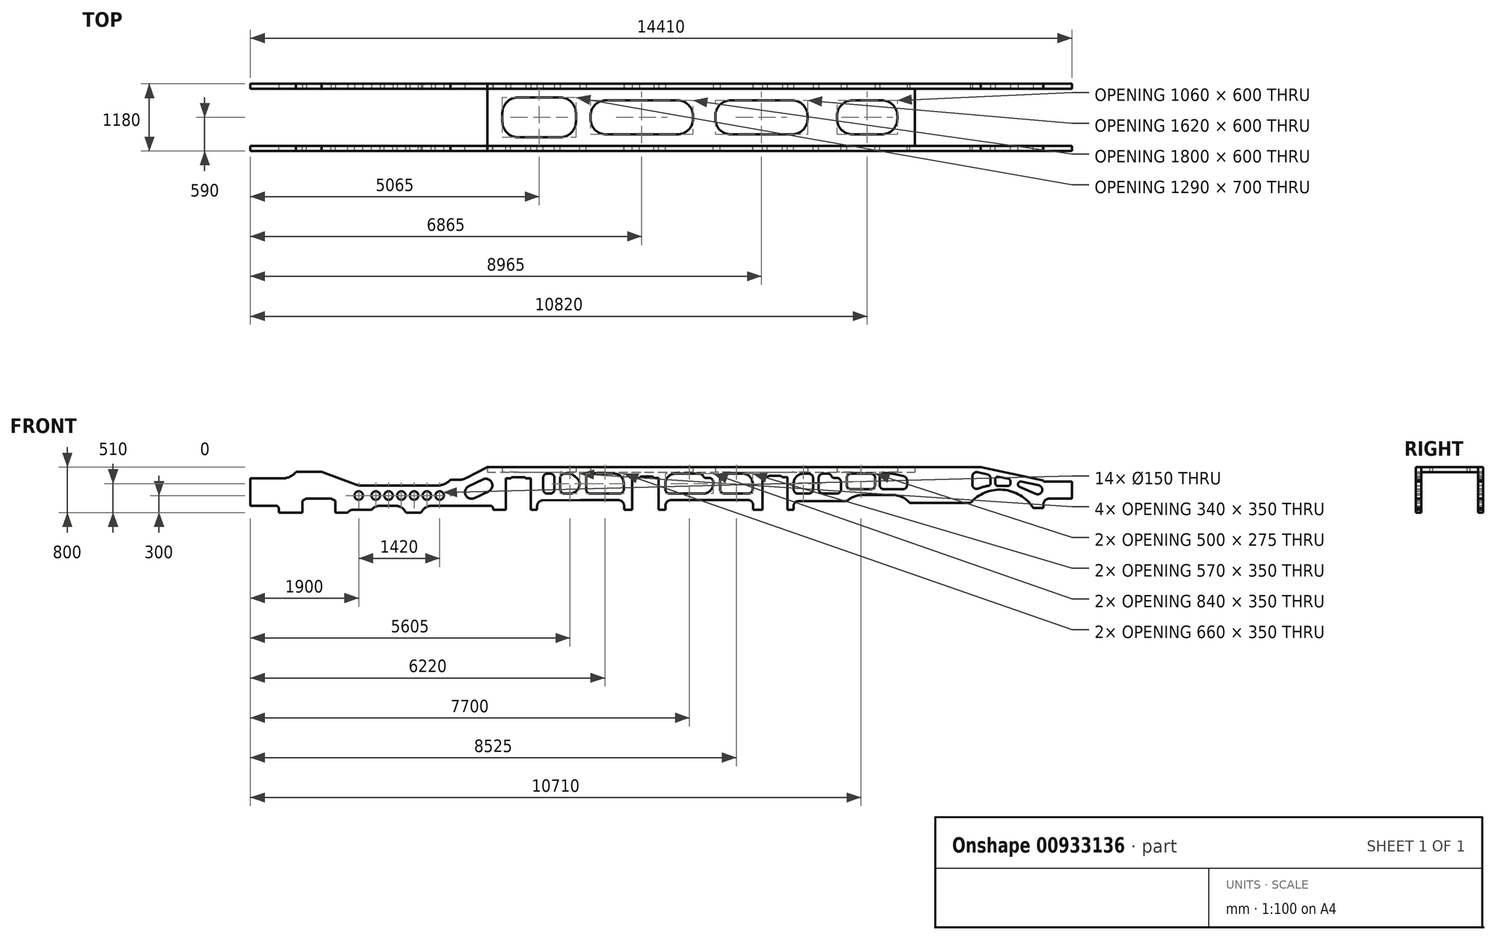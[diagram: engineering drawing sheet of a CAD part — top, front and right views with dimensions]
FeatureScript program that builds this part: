
annotation { "Feature Type Name" : "Feature", "Feature Type Description" : "" }
export const myFeature = defineFeature(function(context is Context, id is Id, definition is map)
    precondition{}
    {
        {
            var Q0;
            Q0=qCreatedBy(makeId("Front.planeOp"),FACE);
            var sketch = newSketch(context, id + "F0", { "sketchPlane" : qUnion([Q0])});
            skLineSegment(sketch, "E0", {"start": v(0, 0) * mm, "end": v(1200, 0) * mm, "construction": true});
            skLineSegment(sketch, "E1", {"start": v(1200, 0) * mm, "end": v(1200, 1949.78) * mm, "construction": true});
            skCircle(sketch, "E2", {"center": v(1200, 625) * mm, "radius": 625 * mm, "construction": true});
            skLineSegment(sketch, "E3", {"start": v(1200, 0) * mm, "end": v(4700, 0) * mm, "construction": true});
            skSolve(sketch);
        }
        {
            var Q0;
            Q0=qCreatedBy(makeId("Front.planeOp"),FACE);
            var sketch = newSketch(context, id + "F1", { "sketchPlane" : qUnion([Q0])});
            skLineSegment(sketch, "E4", {"start": v(800, 1370) * mm, "end": v(1250, 1370) * mm});
            skLineSegment(sketch, "E5", {"start": v(0, 770) * mm, "end": v(450, 770) * mm});
            skLineSegment(sketch, "E6", {"start": v(0, 770) * mm, "end": v(0, 1250) * mm});
            skLineSegment(sketch, "E7", {"start": v(500, 720) * mm, "end": v(500, 650) * mm});
            skLineSegment(sketch, "E8", {"start": v(500, 650) * mm, "end": v(912.5, 650) * mm});
            skLineSegment(sketch, "E9", {"start": v(912.5, 650) * mm, "end": v(912.5, 858.14) * mm});
            skLineSegment(sketch, "E10", {"start": v(912.5, 858.14) * mm, "end": v(985, 900) * mm});
            skLineSegment(sketch, "E11", {"start": v(985, 900) * mm, "end": v(1415, 900) * mm});
            skLineSegment(sketch, "E12", {"start": v(1415, 900) * mm, "end": v(1487.5, 858.14) * mm});
            skLineSegment(sketch, "E13", {"start": v(1487.5, 858.14) * mm, "end": v(1487.5, 650) * mm});
            skLineSegment(sketch, "E14", {"start": v(1487.5, 650) * mm, "end": v(1708.4, 650) * mm});
            skLineSegment(sketch, "E15", {"start": v(1795, 700) * mm, "end": v(2123.01, 700) * mm});
            skLineSegment(sketch, "E16", {"start": v(1200, 0) * mm, "end": v(1200, 1370) * mm, "construction": true});
            skLineSegment(sketch, "E17", {"start": v(2728.3, 650) * mm, "end": v(2996.7, 650) * mm});
            skLineSegment(sketch, "E18", {"start": v(2275, 770) * mm, "end": v(2545, 770) * mm});
            skPoint(sketch, "E19.visualSharp", {"position": v(500, 770) * mm});
            skArc(sketch, "E19.filletArc", {"start": v(500, 720) * mm, "mid": v(485.36, 755.36) * mm, "end": v(450, 770) * mm});
            skArc(sketch, "E20", {"start": v(1708.4, 650) * mm, "mid": v(1745, 686.6) * mm, "end": v(1795, 700) * mm});
            skArc(sketch, "E21", {"start": v(2123.01, 700) * mm, "mid": v(2191.33, 751.66) * mm, "end": v(2275, 770) * mm});
            skArc(sketch, "E22", {"start": v(2728.3, 650) * mm, "mid": v(2654.54, 737.33) * mm, "end": v(2545, 770) * mm});
            skArc(sketch, "E23", {"start": v(2996.7, 650) * mm, "mid": v(3070.46, 737.33) * mm, "end": v(3180, 770) * mm});
            skLineSegment(sketch, "E24", {"start": v(3180, 770) * mm, "end": v(4210, 770) * mm});
            skLineSegment(sketch, "E25", {"start": v(4700, 1450) * mm, "end": v(4700, 0) * mm, "construction": true});
            skLineSegment(sketch, "E26", {"start": v(4155, 1450) * mm, "end": v(12810, 1450) * mm});
            skLineSegment(sketch, "E27", {"start": v(4260, 720) * mm, "end": v(4260, 700) * mm});
            skLineSegment(sketch, "E28", {"start": v(4260, 700) * mm, "end": v(4480, 700) * mm});
            skLineSegment(sketch, "E29", {"start": v(4480, 700) * mm, "end": v(4480, 1250) * mm});
            skLineSegment(sketch, "E30", {"start": v(4480, 1250) * mm, "end": v(4566.7, 1250) * mm});
            skLineSegment(sketch, "E31", {"start": v(4610, 1275) * mm, "end": v(4790, 1275) * mm});
            skLineSegment(sketch, "E32", {"start": v(4833.3, 1250) * mm, "end": v(4920, 1250) * mm});
            skLineSegment(sketch, "E33", {"start": v(4920, 1250) * mm, "end": v(4920, 700) * mm});
            skLineSegment(sketch, "E34", {"start": v(4920, 700) * mm, "end": v(5030, 700) * mm});
            skLineSegment(sketch, "E35", {"start": v(5030, 700) * mm, "end": v(5030, 765.66) * mm});
            skLineSegment(sketch, "E36", {"start": v(5129.34, 865.65) * mm, "end": v(5790, 870) * mm});
            skPoint(sketch, "E37.visualSharp", {"position": v(4260, 770) * mm});
            skArc(sketch, "E37.filletArc", {"start": v(4260, 720) * mm, "mid": v(4245.36, 755.36) * mm, "end": v(4210, 770) * mm});
            skArc(sketch, "E38", {"start": v(4566.7, 1250) * mm, "mid": v(4585, 1268.3) * mm, "end": v(4610, 1275) * mm});
            skArc(sketch, "E39", {"start": v(4833.3, 1250) * mm, "mid": v(4815, 1268.3) * mm, "end": v(4790, 1275) * mm});
            skLineSegment(sketch, "E40", {"start": v(5790, 0) * mm, "end": v(5790, 1450) * mm, "construction": true});
            skPoint(sketch, "E41.visualSharp", {"position": v(5030, 865) * mm});
            skArc(sketch, "E41.filletArc", {"start": v(5129.34, 865.65) * mm, "mid": v(5059.06, 836.13) * mm, "end": v(5030, 765.66) * mm});
            skLineSegment(sketch, "E42", {"start": v(6950, 0) * mm, "end": v(6950, 1450) * mm, "construction": true});
            skLineSegment(sketch, "E43", {"start": v(5790, 870) * mm, "end": v(6455, 870) * mm});
            skLineSegment(sketch, "E44", {"start": v(6555, 770) * mm, "end": v(6555, 700) * mm});
            skLineSegment(sketch, "E45", {"start": v(6555, 700) * mm, "end": v(6700, 700) * mm});
            skLineSegment(sketch, "E46", {"start": v(6700, 700) * mm, "end": v(6700, 1260) * mm});
            skLineSegment(sketch, "E47", {"start": v(6700, 1260) * mm, "end": v(6821.7, 1260) * mm});
            skLineSegment(sketch, "E48", {"start": v(6865, 1285) * mm, "end": v(7035, 1285) * mm});
            skLineSegment(sketch, "E49", {"start": v(7078.3, 1260) * mm, "end": v(7160, 1260) * mm});
            skLineSegment(sketch, "E50", {"start": v(7160, 1260) * mm, "end": v(7160, 700) * mm});
            skLineSegment(sketch, "E51", {"start": v(7160, 700) * mm, "end": v(7280, 700) * mm});
            skLineSegment(sketch, "E52", {"start": v(7280, 700) * mm, "end": v(7280, 770.6) * mm});
            skLineSegment(sketch, "E53", {"start": v(7379.4, 870.6) * mm, "end": v(8110, 875) * mm});
            skPoint(sketch, "E54.visualSharp", {"position": v(7280, 870) * mm});
            skArc(sketch, "E54.filletArc", {"start": v(7379.4, 870.6) * mm, "mid": v(7309.08, 841.1) * mm, "end": v(7280, 770.6) * mm});
            skPoint(sketch, "E55.visualSharp", {"position": v(6555, 870) * mm});
            skArc(sketch, "E55.filletArc", {"start": v(6555, 770) * mm, "mid": v(6525.71, 840.71) * mm, "end": v(6455, 870) * mm});
            skArc(sketch, "E56", {"start": v(6821.7, 1260) * mm, "mid": v(6840, 1278.3) * mm, "end": v(6865, 1285) * mm});
            skArc(sketch, "E57", {"start": v(7078.3, 1260) * mm, "mid": v(7060, 1278.3) * mm, "end": v(7035, 1285) * mm});
            skLineSegment(sketch, "E58", {"start": v(9200, 0) * mm, "end": v(9200, 1450) * mm, "construction": true});
            skLineSegment(sketch, "E59", {"start": v(8110, 0) * mm, "end": v(8110, 1450) * mm, "construction": true});
            skLineSegment(sketch, "E60", {"start": v(8110, 875) * mm, "end": v(8720, 875) * mm});
            skLineSegment(sketch, "E61", {"start": v(8820, 775) * mm, "end": v(8820, 700) * mm});
            skLineSegment(sketch, "E62", {"start": v(8820, 700) * mm, "end": v(8980, 700) * mm});
            skLineSegment(sketch, "E63", {"start": v(8980, 700) * mm, "end": v(8980, 1270) * mm});
            skLineSegment(sketch, "E64", {"start": v(8980, 1270) * mm, "end": v(9066.7, 1270) * mm});
            skLineSegment(sketch, "E65", {"start": v(9110, 1295) * mm, "end": v(9290, 1295) * mm});
            skLineSegment(sketch, "E66", {"start": v(9333.3, 1270) * mm, "end": v(9420, 1270) * mm});
            skLineSegment(sketch, "E67", {"start": v(9420, 1270) * mm, "end": v(9420, 700) * mm});
            skLineSegment(sketch, "E68", {"start": v(9420, 700) * mm, "end": v(9530, 700) * mm});
            skLineSegment(sketch, "E69", {"start": v(9530, 700) * mm, "end": v(9530, 775) * mm});
            skLineSegment(sketch, "E70", {"start": v(9605, 850) * mm, "end": v(10459.5, 850) * mm});
            skPoint(sketch, "E71.visualSharp", {"position": v(8820, 875) * mm});
            skArc(sketch, "E71.filletArc", {"start": v(8820, 775) * mm, "mid": v(8790.71, 845.71) * mm, "end": v(8720, 875) * mm});
            skPoint(sketch, "E72.visualSharp", {"position": v(9530, 850) * mm});
            skArc(sketch, "E72.filletArc", {"start": v(9605, 850) * mm, "mid": v(9551.97, 828.03) * mm, "end": v(9530, 775) * mm});
            skArc(sketch, "E73", {"start": v(9066.7, 1270) * mm, "mid": v(9085, 1288.3) * mm, "end": v(9110, 1295) * mm});
            skArc(sketch, "E74", {"start": v(9333.3, 1270) * mm, "mid": v(9315, 1288.3) * mm, "end": v(9290, 1295) * mm});
            skLineSegment(sketch, "E75", {"start": v(11000, 0) * mm, "end": v(11000, 1450) * mm, "construction": true});
            skLineSegment(sketch, "E76", {"start": v(12100, 0) * mm, "end": v(12100, 1450) * mm, "construction": true});
            skLineSegment(sketch, "E77", {"start": v(13200, 0) * mm, "end": v(13200, 1366.68) * mm, "construction": true});
            skLineSegment(sketch, "E78", {"start": v(10735, 960) * mm, "end": v(11265, 960) * mm});
            skLineSegment(sketch, "E79", {"start": v(11568.97, 820) * mm, "end": v(12631.03, 820) * mm});
            skArc(sketch, "E80", {"start": v(10459.5, 850) * mm, "mid": v(10586.68, 931.48) * mm, "end": v(10735, 960) * mm});
            skArc(sketch, "E81", {"start": v(11568.97, 820) * mm, "mid": v(11432.33, 923.32) * mm, "end": v(11265, 960) * mm});
            skLineSegment(sketch, "E82", {"start": v(13730, 735) * mm, "end": v(13910, 735) * mm});
            skLineSegment(sketch, "E83", {"start": v(13910, 735) * mm, "end": v(13910, 795) * mm});
            skLineSegment(sketch, "E84", {"start": v(14010, 895) * mm, "end": v(14410, 895) * mm});
            skLineSegment(sketch, "E85", {"start": v(14410, 895) * mm, "end": v(14410, 1195) * mm});
            skLineSegment(sketch, "E86", {"start": v(14410, 1195) * mm, "end": v(13910, 1195) * mm});
            skLineSegment(sketch, "E87", {"start": v(13910, 1195) * mm, "end": v(13910, 1215) * mm});
            skLineSegment(sketch, "E88", {"start": v(13910, 1215) * mm, "end": v(12810, 1450) * mm});
            skArc(sketch, "E89", {"start": v(12631.03, 820) * mm, "mid": v(13201.7, 1051.52) * mm, "end": v(13730, 735) * mm});
            skPoint(sketch, "E90.visualSharp", {"position": v(13910, 895) * mm});
            skArc(sketch, "E90.filletArc", {"start": v(14010, 895) * mm, "mid": v(13939.29, 865.71) * mm, "end": v(13910, 795) * mm});
            skLineSegment(sketch, "E91", {"start": v(0, 1250) * mm, "end": v(560, 1250) * mm});
            skArc(sketch, "E92", {"start": v(560, 1250) * mm, "mid": v(694.16, 1281.67) * mm, "end": v(800, 1370) * mm});
            skLineSegment(sketch, "E93", {"start": v(1250, 1370) * mm, "end": v(1843.46, 1144.55) * mm});
            skLineSegment(sketch, "E94", {"start": v(1950, 1125) * mm, "end": v(3275, 1125) * mm});
            skLineSegment(sketch, "E95", {"start": v(3509.52, 1225) * mm, "end": v(3650, 1225) * mm});
            skLineSegment(sketch, "E96", {"start": v(3788.71, 1259) * mm, "end": v(4155, 1450) * mm});
            skPoint(sketch, "E97.visualSharp", {"position": v(1894.94, 1125) * mm});
            skArc(sketch, "E97.filletArc", {"start": v(1843.46, 1144.55) * mm, "mid": v(1895.84, 1129.93) * mm, "end": v(1950, 1125) * mm});
            skPoint(sketch, "E98.visualSharp", {"position": v(3723.52, 1225) * mm});
            skArc(sketch, "E98.filletArc", {"start": v(3650, 1225) * mm, "mid": v(3721.4, 1233.62) * mm, "end": v(3788.71, 1259) * mm});
            skArc(sketch, "E99", {"start": v(3275, 1125) * mm, "mid": v(3402.48, 1151.04) * mm, "end": v(3509.52, 1225) * mm});
            skLineSegment(sketch, "E100", {"start": v(1900, 950) * mm, "end": v(3320, 950) * mm, "construction": true});
            skCircle(sketch, "E101", {"center": v(1900, 950) * mm, "radius": 75 * mm});
            skCircle(sketch, "E102", {"center": v(2200, 950) * mm, "radius": 75 * mm});
            skCircle(sketch, "E103", {"center": v(2424, 950) * mm, "radius": 75 * mm});
            skCircle(sketch, "E104", {"center": v(2648, 950) * mm, "radius": 75 * mm});
            skCircle(sketch, "E105", {"center": v(2872, 950) * mm, "radius": 75 * mm});
            skCircle(sketch, "E106", {"center": v(3096, 950) * mm, "radius": 75 * mm});
            skCircle(sketch, "E107", {"center": v(3320, 950) * mm, "radius": 75 * mm});
            skLineSegment(sketch, "E108", {"start": v(3880, 1010) * mm, "end": v(4130, 1130) * mm, "construction": true});
            skArc(sketch, "E109.0.startCap", {"start": v(3929.76, 906.32) * mm, "mid": v(3776.32, 960.24) * mm, "end": v(3830.24, 1113.68) * mm});
            skArc(sketch, "E109.0.endCap", {"start": v(4080.24, 1233.68) * mm, "mid": v(4233.68, 1179.76) * mm, "end": v(4179.76, 1026.32) * mm});
            skLineSegment(sketch, "E109.0.left", {"start": v(3830.24, 1113.68) * mm, "end": v(4080.24, 1233.68) * mm});
            skLineSegment(sketch, "E109.0.right", {"start": v(3929.76, 906.32) * mm, "end": v(4179.76, 1026.32) * mm});
            skLineSegment(sketch, "E110.bottom", {"start": v(5210, 1335) * mm, "end": v(5260, 1335) * mm});
            skLineSegment(sketch, "E110.top", {"start": v(5210, 985) * mm, "end": v(5260, 985) * mm});
            skLineSegment(sketch, "E110.left", {"start": v(5135, 1260) * mm, "end": v(5135, 1060) * mm});
            skLineSegment(sketch, "E110.right", {"start": v(5335, 1260) * mm, "end": v(5335, 1060) * mm});
            skLineSegment(sketch, "E111.bottom", {"start": v(5965, 1335) * mm, "end": v(6375, 1335) * mm});
            skLineSegment(sketch, "E111.top", {"start": v(5965, 985) * mm, "end": v(6475, 985) * mm});
            skLineSegment(sketch, "E111.left", {"start": v(5890, 1260) * mm, "end": v(5890, 1060) * mm});
            skLineSegment(sketch, "E111.right", {"start": v(6550, 1160) * mm, "end": v(6550, 1060) * mm});
            skPoint(sketch, "E112.visualSharp", {"position": v(5135, 1335) * mm});
            skArc(sketch, "E112.filletArc", {"start": v(5210, 1335) * mm, "mid": v(5156.97, 1313.03) * mm, "end": v(5135, 1260) * mm});
            skPoint(sketch, "E113.visualSharp", {"position": v(5335, 1335) * mm});
            skArc(sketch, "E113.filletArc", {"start": v(5335, 1260) * mm, "mid": v(5313.03, 1313.03) * mm, "end": v(5260, 1335) * mm});
            skPoint(sketch, "E114.visualSharp", {"position": v(5135, 985) * mm});
            skArc(sketch, "E114.filletArc", {"start": v(5135, 1060) * mm, "mid": v(5156.97, 1006.97) * mm, "end": v(5210, 985) * mm});
            skPoint(sketch, "E115.visualSharp", {"position": v(5335, 985) * mm});
            skArc(sketch, "E115.filletArc", {"start": v(5260, 985) * mm, "mid": v(5313.03, 1006.97) * mm, "end": v(5335, 1060) * mm});
            skLineSegment(sketch, "E116", {"start": v(5435, 1060) * mm, "end": v(5435, 1260) * mm});
            skLineSegment(sketch, "E117", {"start": v(5510, 1335) * mm, "end": v(5580, 1335) * mm});
            skLineSegment(sketch, "E118", {"start": v(5682.3, 1294.7) * mm, "end": v(5743.2, 1237.91) * mm});
            skLineSegment(sketch, "E119", {"start": v(5775, 1164.78) * mm, "end": v(5775, 1160) * mm});
            skLineSegment(sketch, "E120", {"start": v(5600, 985) * mm, "end": v(5510, 985) * mm});
            skPoint(sketch, "E121.visualSharp", {"position": v(5435, 1335) * mm});
            skArc(sketch, "E121.filletArc", {"start": v(5510, 1335) * mm, "mid": v(5456.97, 1313.03) * mm, "end": v(5435, 1260) * mm});
            skPoint(sketch, "E122.visualSharp", {"position": v(5435, 985) * mm});
            skArc(sketch, "E122.filletArc", {"start": v(5435, 1060) * mm, "mid": v(5456.97, 1006.97) * mm, "end": v(5510, 985) * mm});
            skPoint(sketch, "E123.visualSharp", {"position": v(5639.09, 1335) * mm});
            skArc(sketch, "E123.filletArc", {"start": v(5682.3, 1294.7) * mm, "mid": v(5634.98, 1324.56) * mm, "end": v(5580, 1335) * mm});
            skPoint(sketch, "E124.visualSharp", {"position": v(5775, 985) * mm});
            skArc(sketch, "E124.filletArc", {"start": v(5600, 985) * mm, "mid": v(5723.74, 1036.26) * mm, "end": v(5775, 1160) * mm});
            skPoint(sketch, "E125.visualSharp", {"position": v(5775, 1208.26) * mm});
            skArc(sketch, "E125.filletArc", {"start": v(5775, 1164.78) * mm, "mid": v(5766.7, 1204.65) * mm, "end": v(5743.2, 1237.91) * mm});
            skPoint(sketch, "E126.visualSharp", {"position": v(5890, 1335) * mm});
            skArc(sketch, "E126.filletArc", {"start": v(5965, 1335) * mm, "mid": v(5911.97, 1313.03) * mm, "end": v(5890, 1260) * mm});
            skPoint(sketch, "E127.visualSharp", {"position": v(5890, 985) * mm});
            skArc(sketch, "E127.filletArc", {"start": v(5890, 1060) * mm, "mid": v(5911.97, 1006.97) * mm, "end": v(5965, 985) * mm});
            skPoint(sketch, "E128.visualSharp", {"position": v(6550, 985) * mm});
            skArc(sketch, "E128.filletArc", {"start": v(6475, 985) * mm, "mid": v(6528.03, 1006.97) * mm, "end": v(6550, 1060) * mm});
            skPoint(sketch, "E129.visualSharp", {"position": v(6550, 1335) * mm});
            skArc(sketch, "E129.filletArc", {"start": v(6550, 1160) * mm, "mid": v(6498.74, 1283.74) * mm, "end": v(6375, 1335) * mm});
            skLineSegment(sketch, "E130", {"start": v(7280, 1060) * mm, "end": v(7280, 1160) * mm});
            skLineSegment(sketch, "E131", {"start": v(7455, 1335) * mm, "end": v(7875.44, 1335) * mm});
            skLineSegment(sketch, "E132", {"start": v(7355, 985) * mm, "end": v(7945, 985) * mm});
            skLineSegment(sketch, "E133", {"start": v(8120, 1160) * mm, "end": v(8120, 1185) * mm});
            skLineSegment(sketch, "E134", {"start": v(8045, 1260) * mm, "end": v(7990, 1260) * mm});
            skArc(sketch, "E135", {"start": v(7990, 1260) * mm, "mid": v(7962.61, 1268.17) * mm, "end": v(7944.17, 1290) * mm});
            skArc(sketch, "E136", {"start": v(7875.44, 1335) * mm, "mid": v(7916.51, 1322.75) * mm, "end": v(7944.17, 1290) * mm});
            skPoint(sketch, "E137.visualSharp", {"position": v(7280, 1335) * mm});
            skArc(sketch, "E137.filletArc", {"start": v(7455, 1335) * mm, "mid": v(7331.26, 1283.74) * mm, "end": v(7280, 1160) * mm});
            skPoint(sketch, "E138.visualSharp", {"position": v(7280, 985) * mm});
            skArc(sketch, "E138.filletArc", {"start": v(7280, 1060) * mm, "mid": v(7301.97, 1006.97) * mm, "end": v(7355, 985) * mm});
            skPoint(sketch, "E139.visualSharp", {"position": v(8120, 1260) * mm});
            skArc(sketch, "E139.filletArc", {"start": v(8120, 1185) * mm, "mid": v(8098.03, 1238.03) * mm, "end": v(8045, 1260) * mm});
            skPoint(sketch, "E140.visualSharp", {"position": v(8120, 985) * mm});
            skArc(sketch, "E140.filletArc", {"start": v(7945, 985) * mm, "mid": v(8068.74, 1036.26) * mm, "end": v(8120, 1160) * mm});
            skLineSegment(sketch, "E141.bottom", {"start": v(8315, 1335) * mm, "end": v(8635, 1335) * mm});
            skLineSegment(sketch, "E141.top", {"start": v(8315, 985) * mm, "end": v(8735, 985) * mm});
            skLineSegment(sketch, "E141.left", {"start": v(8240, 1260) * mm, "end": v(8240, 1060) * mm});
            skLineSegment(sketch, "E141.right", {"start": v(8810, 1160) * mm, "end": v(8810, 1060) * mm});
            skPoint(sketch, "E142.visualSharp", {"position": v(8810, 1335) * mm});
            skArc(sketch, "E142.filletArc", {"start": v(8810, 1160) * mm, "mid": v(8758.74, 1283.74) * mm, "end": v(8635, 1335) * mm});
            skPoint(sketch, "E143.visualSharp", {"position": v(8810, 985) * mm});
            skArc(sketch, "E143.filletArc", {"start": v(8735, 985) * mm, "mid": v(8788.03, 1006.97) * mm, "end": v(8810, 1060) * mm});
            skPoint(sketch, "E144.visualSharp", {"position": v(8240, 985) * mm});
            skArc(sketch, "E144.filletArc", {"start": v(8240, 1060) * mm, "mid": v(8261.97, 1006.97) * mm, "end": v(8315, 985) * mm});
            skPoint(sketch, "E145.visualSharp", {"position": v(8240, 1335) * mm});
            skArc(sketch, "E145.filletArc", {"start": v(8315, 1335) * mm, "mid": v(8261.97, 1313.03) * mm, "end": v(8240, 1260) * mm});
            skLineSegment(sketch, "E146.bottom", {"start": v(9705, 1335) * mm, "end": v(9795, 1335) * mm});
            skLineSegment(sketch, "E146.top", {"start": v(9605, 985) * mm, "end": v(9795, 985) * mm});
            skLineSegment(sketch, "E146.left", {"start": v(9530, 1160) * mm, "end": v(9530, 1060) * mm});
            skLineSegment(sketch, "E146.right", {"start": v(9870, 1260) * mm, "end": v(9870, 1060) * mm});
            skPoint(sketch, "E147.visualSharp", {"position": v(9530, 985) * mm});
            skArc(sketch, "E147.filletArc", {"start": v(9530, 1060) * mm, "mid": v(9551.97, 1006.97) * mm, "end": v(9605, 985) * mm});
            skPoint(sketch, "E148.visualSharp", {"position": v(9870, 985) * mm});
            skArc(sketch, "E148.filletArc", {"start": v(9795, 985) * mm, "mid": v(9848.03, 1006.97) * mm, "end": v(9870, 1060) * mm});
            skPoint(sketch, "E149.visualSharp", {"position": v(9870, 1335) * mm});
            skArc(sketch, "E149.filletArc", {"start": v(9870, 1260) * mm, "mid": v(9848.03, 1313.03) * mm, "end": v(9795, 1335) * mm});
            skPoint(sketch, "E150.visualSharp", {"position": v(9530, 1335) * mm});
            skArc(sketch, "E150.filletArc", {"start": v(9705, 1335) * mm, "mid": v(9581.26, 1283.74) * mm, "end": v(9530, 1160) * mm});
            skLineSegment(sketch, "E151", {"start": v(10125.44, 1335) * mm, "end": v(10045, 1335) * mm});
            skLineSegment(sketch, "E152", {"start": v(9970, 1260) * mm, "end": v(9970, 1060) * mm});
            skLineSegment(sketch, "E153", {"start": v(10045, 985) * mm, "end": v(10285, 985) * mm});
            skLineSegment(sketch, "E154", {"start": v(10360, 1060) * mm, "end": v(10360, 1185) * mm});
            skLineSegment(sketch, "E155", {"start": v(10240, 1260) * mm, "end": v(10285, 1260) * mm});
            skPoint(sketch, "E156.visualSharp", {"position": v(9970, 985) * mm});
            skArc(sketch, "E156.filletArc", {"start": v(9970, 1060) * mm, "mid": v(9991.97, 1006.97) * mm, "end": v(10045, 985) * mm});
            skPoint(sketch, "E157.visualSharp", {"position": v(10360, 985) * mm});
            skArc(sketch, "E157.filletArc", {"start": v(10285, 985) * mm, "mid": v(10338.03, 1006.97) * mm, "end": v(10360, 1060) * mm});
            skPoint(sketch, "E158.visualSharp", {"position": v(9970, 1335) * mm});
            skArc(sketch, "E158.filletArc", {"start": v(10045, 1335) * mm, "mid": v(9991.97, 1313.03) * mm, "end": v(9970, 1260) * mm});
            skPoint(sketch, "E159.visualSharp", {"position": v(10360, 1260) * mm});
            skArc(sketch, "E159.filletArc", {"start": v(10360, 1185) * mm, "mid": v(10338.03, 1238.03) * mm, "end": v(10285, 1260) * mm});
            skArc(sketch, "E160", {"start": v(10240, 1260) * mm, "mid": v(10212.61, 1268.17) * mm, "end": v(10194.17, 1290) * mm});
            skArc(sketch, "E161", {"start": v(10125.44, 1335) * mm, "mid": v(10166.51, 1322.75) * mm, "end": v(10194.17, 1290) * mm});
            skLineSegment(sketch, "E162.bottom", {"start": v(10535, 1335) * mm, "end": v(10885, 1335) * mm});
            skLineSegment(sketch, "E162.top", {"start": v(10535, 1060) * mm, "end": v(10885, 1060) * mm});
            skLineSegment(sketch, "E162.left", {"start": v(10460, 1260) * mm, "end": v(10460, 1135) * mm});
            skLineSegment(sketch, "E162.right", {"start": v(10960, 1260) * mm, "end": v(10960, 1135) * mm});
            skPoint(sketch, "E163.visualSharp", {"position": v(10460, 1335) * mm});
            skArc(sketch, "E163.filletArc", {"start": v(10535, 1335) * mm, "mid": v(10481.97, 1313.03) * mm, "end": v(10460, 1260) * mm});
            skPoint(sketch, "E164.visualSharp", {"position": v(10460, 1060) * mm});
            skArc(sketch, "E164.filletArc", {"start": v(10460, 1135) * mm, "mid": v(10481.97, 1081.97) * mm, "end": v(10535, 1060) * mm});
            skPoint(sketch, "E165.visualSharp", {"position": v(10960, 1060) * mm});
            skArc(sketch, "E165.filletArc", {"start": v(10885, 1060) * mm, "mid": v(10938.03, 1081.97) * mm, "end": v(10960, 1135) * mm});
            skPoint(sketch, "E166.visualSharp", {"position": v(10960, 1335) * mm});
            skArc(sketch, "E166.filletArc", {"start": v(10960, 1260) * mm, "mid": v(10938.03, 1313.03) * mm, "end": v(10885, 1335) * mm});
            skLineSegment(sketch, "E167", {"start": v(11245, 1335) * mm, "end": v(11115, 1335) * mm});
            skLineSegment(sketch, "E168", {"start": v(11040, 1260) * mm, "end": v(11040, 1135) * mm});
            skLineSegment(sketch, "E169", {"start": v(11115, 1060) * mm, "end": v(11445, 1060) * mm});
            skLineSegment(sketch, "E170", {"start": v(11520, 1135) * mm, "end": v(11520, 1215) * mm});
            skLineSegment(sketch, "E171", {"start": v(11461.46, 1288.17) * mm, "end": v(11261.46, 1333.17) * mm});
            skPoint(sketch, "E172.visualSharp", {"position": v(11040, 1060) * mm});
            skArc(sketch, "E172.filletArc", {"start": v(11040, 1135) * mm, "mid": v(11061.97, 1081.97) * mm, "end": v(11115, 1060) * mm});
            skPoint(sketch, "E173.visualSharp", {"position": v(11520, 1060) * mm});
            skArc(sketch, "E173.filletArc", {"start": v(11445, 1060) * mm, "mid": v(11498.03, 1081.97) * mm, "end": v(11520, 1135) * mm});
            skPoint(sketch, "E174.visualSharp", {"position": v(11520, 1275) * mm});
            skArc(sketch, "E174.filletArc", {"start": v(11520, 1215) * mm, "mid": v(11503.57, 1261.85) * mm, "end": v(11461.46, 1288.17) * mm});
            skPoint(sketch, "E175.visualSharp", {"position": v(11040, 1335) * mm});
            skArc(sketch, "E175.filletArc", {"start": v(11115, 1335) * mm, "mid": v(11061.97, 1313.03) * mm, "end": v(11040, 1260) * mm});
            skPoint(sketch, "E176.visualSharp", {"position": v(11253.33, 1335) * mm});
            skArc(sketch, "E176.filletArc", {"start": v(11261.46, 1333.17) * mm, "mid": v(11253.28, 1334.54) * mm, "end": v(11245, 1335) * mm});
            skLineSegment(sketch, "E177", {"start": v(12755.67, 1359.35) * mm, "end": v(12925.67, 1323.03) * mm});
            skLineSegment(sketch, "E178", {"start": v(12985, 1249.69) * mm, "end": v(12985, 1169.69) * mm});
            skLineSegment(sketch, "E179", {"start": v(12665, 1286) * mm, "end": v(12665, 1141.68) * mm});
            skLineSegment(sketch, "E180.bottom", {"start": v(13125.45, 1280.35) * mm, "end": v(13295.45, 1244.03) * mm});
            skLineSegment(sketch, "E180.top", {"start": v(13115, 1120.14) * mm, "end": v(13285, 1120.14) * mm});
            skLineSegment(sketch, "E180.left", {"start": v(13065, 1231.46) * mm, "end": v(13065, 1170.14) * mm});
            skLineSegment(sketch, "E180.right", {"start": v(13335, 1195.14) * mm, "end": v(13335, 1170.14) * mm});
            skArc(sketch, "E181", {"start": v(12768.24, 1072.2) * mm, "mid": v(12854, 1101.33) * mm, "end": v(12942.58, 1120.26) * mm});
            skLineSegment(sketch, "E182", {"start": v(12985, 1310.36) * mm, "end": v(13065, 1293.27) * mm, "construction": true});
            skPoint(sketch, "E183.visualSharp", {"position": v(12665, 1378.72) * mm});
            skArc(sketch, "E183.filletArc", {"start": v(12755.67, 1359.35) * mm, "mid": v(12692.83, 1344.32) * mm, "end": v(12665, 1286) * mm});
            skPoint(sketch, "E184.visualSharp", {"position": v(12985, 1310.36) * mm});
            skArc(sketch, "E184.filletArc", {"start": v(12985, 1249.69) * mm, "mid": v(12968.31, 1296.86) * mm, "end": v(12925.67, 1323.03) * mm});
            skArc(sketch, "E185", {"start": v(12985, 1169.69) * mm, "mid": v(12972.94, 1137.12) * mm, "end": v(12942.58, 1120.26) * mm});
            skArc(sketch, "E186", {"start": v(12665, 1141.68) * mm, "mid": v(12698.12, 1079.46) * mm, "end": v(12768.24, 1072.2) * mm});
            skPoint(sketch, "E187.visualSharp", {"position": v(13065, 1120.14) * mm});
            skArc(sketch, "E187.filletArc", {"start": v(13065, 1170.14) * mm, "mid": v(13079.64, 1134.78) * mm, "end": v(13115, 1120.14) * mm});
            skPoint(sketch, "E188.visualSharp", {"position": v(13065, 1293.27) * mm});
            skArc(sketch, "E188.filletArc", {"start": v(13125.45, 1280.35) * mm, "mid": v(13083.55, 1270.33) * mm, "end": v(13065, 1231.46) * mm});
            skPoint(sketch, "E189.visualSharp", {"position": v(13335, 1235.58) * mm});
            skArc(sketch, "E189.filletArc", {"start": v(13335, 1195.14) * mm, "mid": v(13323.87, 1226.58) * mm, "end": v(13295.45, 1244.03) * mm});
            skPoint(sketch, "E190.visualSharp", {"position": v(13335, 1120.14) * mm});
            skArc(sketch, "E190.filletArc", {"start": v(13285, 1120.14) * mm, "mid": v(13320.36, 1134.78) * mm, "end": v(13335, 1170.14) * mm});
            skLineSegment(sketch, "E191", {"start": v(13335, 1235.58) * mm, "end": v(13525.26, 1194.94) * mm, "construction": true});
            skLineSegment(sketch, "E192", {"start": v(13525.26, 1194.94) * mm, "end": v(13828.42, 1130.17) * mm});
            skLineSegment(sketch, "E193", {"start": v(13495.19, 1100.06) * mm, "end": v(13780.3, 978.36) * mm});
            skArc(sketch, "E194", {"start": v(13525.26, 1194.94) * mm, "mid": v(13467.15, 1161.15) * mm, "end": v(13495.19, 1100.06) * mm});
            skArc(sketch, "E195", {"start": v(13828.42, 1130.17) * mm, "mid": v(13887.97, 1027.77) * mm, "end": v(13780.3, 978.36) * mm});
            skSolve(sketch);
        }
        {
            var Q0;
            Q0=makeQuery(id+"F1.imprint","IMPRINT",FACE,{"disambiguationData":[TD([[makeQuery(id+"F1.imprint","IMPRINT",EDGE,{"derivedFrom":sQuery(id+"F1.wireOp",EDGE,"E4")}),-1.0]])]});
            extrude(context, id + "F2", {"entities" : qUnion([Q0]), "depth" : 590 * mm, "offsetDistance" : 25 * mm, "hasSecondDirection" : true, "secondDirectionOppositeDirection" : false, "secondDirectionDepth" : 500 * mm});
        }
        {
            var Q0;
            Q0=makeQuery(id+"F2.opExtrude","SWEPT_BODY",BODY,{"disambiguationData":[OSD([sQuery(id+"F1.wireOp",EDGE,"E4"),sQuery(id+"F1.wireOp",EDGE,"E5"),sQuery(id+"F1.wireOp",EDGE,"E6"),sQuery(id+"F1.wireOp",EDGE,"E7"),sQuery(id+"F1.wireOp",EDGE,"E8"),sQuery(id+"F1.wireOp",EDGE,"E9"),sQuery(id+"F1.wireOp",EDGE,"E10"),sQuery(id+"F1.wireOp",EDGE,"E11"),sQuery(id+"F1.wireOp",EDGE,"E12"),sQuery(id+"F1.wireOp",EDGE,"E13"),sQuery(id+"F1.wireOp",EDGE,"E14"),sQuery(id+"F1.wireOp",EDGE,"E15"),sQuery(id+"F1.wireOp",EDGE,"E17"),sQuery(id+"F1.wireOp",EDGE,"E18"),sQuery(id+"F1.wireOp",EDGE,"E19.filletArc"),sQuery(id+"F1.wireOp",EDGE,"E20"),sQuery(id+"F1.wireOp",EDGE,"E21"),sQuery(id+"F1.wireOp",EDGE,"E22"),sQuery(id+"F1.wireOp",EDGE,"E23"),sQuery(id+"F1.wireOp",EDGE,"E24"),sQuery(id+"F1.wireOp",EDGE,"E26"),sQuery(id+"F1.wireOp",EDGE,"E27"),sQuery(id+"F1.wireOp",EDGE,"E28"),sQuery(id+"F1.wireOp",EDGE,"E29"),sQuery(id+"F1.wireOp",EDGE,"E30"),sQuery(id+"F1.wireOp",EDGE,"E31"),sQuery(id+"F1.wireOp",EDGE,"E32"),sQuery(id+"F1.wireOp",EDGE,"E33"),sQuery(id+"F1.wireOp",EDGE,"E34"),sQuery(id+"F1.wireOp",EDGE,"E35"),sQuery(id+"F1.wireOp",EDGE,"E36"),sQuery(id+"F1.wireOp",EDGE,"E37.filletArc"),sQuery(id+"F1.wireOp",EDGE,"E38"),sQuery(id+"F1.wireOp",EDGE,"E39"),sQuery(id+"F1.wireOp",EDGE,"E41.filletArc"),sQuery(id+"F1.wireOp",EDGE,"E43"),sQuery(id+"F1.wireOp",EDGE,"E44"),sQuery(id+"F1.wireOp",EDGE,"E45"),sQuery(id+"F1.wireOp",EDGE,"E46"),sQuery(id+"F1.wireOp",EDGE,"E47"),sQuery(id+"F1.wireOp",EDGE,"E48"),sQuery(id+"F1.wireOp",EDGE,"E49"),sQuery(id+"F1.wireOp",EDGE,"E50"),sQuery(id+"F1.wireOp",EDGE,"E51"),sQuery(id+"F1.wireOp",EDGE,"E52"),sQuery(id+"F1.wireOp",EDGE,"E53"),sQuery(id+"F1.wireOp",EDGE,"E54.filletArc"),sQuery(id+"F1.wireOp",EDGE,"E55.filletArc"),sQuery(id+"F1.wireOp",EDGE,"E56"),sQuery(id+"F1.wireOp",EDGE,"E57"),sQuery(id+"F1.wireOp",EDGE,"E60"),sQuery(id+"F1.wireOp",EDGE,"E61"),sQuery(id+"F1.wireOp",EDGE,"E62"),sQuery(id+"F1.wireOp",EDGE,"E63"),sQuery(id+"F1.wireOp",EDGE,"E64"),sQuery(id+"F1.wireOp",EDGE,"E65"),sQuery(id+"F1.wireOp",EDGE,"E66"),sQuery(id+"F1.wireOp",EDGE,"E67"),sQuery(id+"F1.wireOp",EDGE,"E68"),sQuery(id+"F1.wireOp",EDGE,"E69"),sQuery(id+"F1.wireOp",EDGE,"E70"),sQuery(id+"F1.wireOp",EDGE,"E71.filletArc"),sQuery(id+"F1.wireOp",EDGE,"E72.filletArc"),sQuery(id+"F1.wireOp",EDGE,"E73"),sQuery(id+"F1.wireOp",EDGE,"E74"),sQuery(id+"F1.wireOp",EDGE,"E78"),sQuery(id+"F1.wireOp",EDGE,"E79"),sQuery(id+"F1.wireOp",EDGE,"E80"),sQuery(id+"F1.wireOp",EDGE,"E81"),sQuery(id+"F1.wireOp",EDGE,"E82"),sQuery(id+"F1.wireOp",EDGE,"E83"),sQuery(id+"F1.wireOp",EDGE,"E84"),sQuery(id+"F1.wireOp",EDGE,"E85"),sQuery(id+"F1.wireOp",EDGE,"E86"),sQuery(id+"F1.wireOp",EDGE,"E87"),sQuery(id+"F1.wireOp",EDGE,"E88"),sQuery(id+"F1.wireOp",EDGE,"E89"),sQuery(id+"F1.wireOp",EDGE,"E90.filletArc"),sQuery(id+"F1.wireOp",EDGE,"E91"),sQuery(id+"F1.wireOp",EDGE,"E92"),sQuery(id+"F1.wireOp",EDGE,"E93"),sQuery(id+"F1.wireOp",EDGE,"E94"),sQuery(id+"F1.wireOp",EDGE,"E95"),sQuery(id+"F1.wireOp",EDGE,"E96"),sQuery(id+"F1.wireOp",EDGE,"E97.filletArc"),sQuery(id+"F1.wireOp",EDGE,"E98.filletArc"),sQuery(id+"F1.wireOp",EDGE,"E99"),sQuery(id+"F1.wireOp",EDGE,"E101"),sQuery(id+"F1.wireOp",EDGE,"E102"),sQuery(id+"F1.wireOp",EDGE,"E103"),sQuery(id+"F1.wireOp",EDGE,"E104"),sQuery(id+"F1.wireOp",EDGE,"E105"),sQuery(id+"F1.wireOp",EDGE,"E106"),sQuery(id+"F1.wireOp",EDGE,"E107"),sQuery(id+"F1.wireOp",EDGE,"E109.0.startCap"),sQuery(id+"F1.wireOp",EDGE,"E109.0.endCap"),sQuery(id+"F1.wireOp",EDGE,"E109.0.left"),sQuery(id+"F1.wireOp",EDGE,"E109.0.right"),sQuery(id+"F1.wireOp",EDGE,"E110.bottom"),sQuery(id+"F1.wireOp",EDGE,"E110.top"),sQuery(id+"F1.wireOp",EDGE,"E110.left"),sQuery(id+"F1.wireOp",EDGE,"E110.right"),sQuery(id+"F1.wireOp",EDGE,"E111.bottom"),sQuery(id+"F1.wireOp",EDGE,"E111.top"),sQuery(id+"F1.wireOp",EDGE,"E111.left"),sQuery(id+"F1.wireOp",EDGE,"E111.right"),sQuery(id+"F1.wireOp",EDGE,"E112.filletArc"),sQuery(id+"F1.wireOp",EDGE,"E113.filletArc"),sQuery(id+"F1.wireOp",EDGE,"E114.filletArc"),sQuery(id+"F1.wireOp",EDGE,"E115.filletArc"),sQuery(id+"F1.wireOp",EDGE,"E116"),sQuery(id+"F1.wireOp",EDGE,"E117"),sQuery(id+"F1.wireOp",EDGE,"E118"),sQuery(id+"F1.wireOp",EDGE,"E119"),sQuery(id+"F1.wireOp",EDGE,"E120"),sQuery(id+"F1.wireOp",EDGE,"E121.filletArc"),sQuery(id+"F1.wireOp",EDGE,"E122.filletArc"),sQuery(id+"F1.wireOp",EDGE,"E123.filletArc"),sQuery(id+"F1.wireOp",EDGE,"E124.filletArc"),sQuery(id+"F1.wireOp",EDGE,"E125.filletArc"),sQuery(id+"F1.wireOp",EDGE,"E126.filletArc"),sQuery(id+"F1.wireOp",EDGE,"E127.filletArc"),sQuery(id+"F1.wireOp",EDGE,"E128.filletArc"),sQuery(id+"F1.wireOp",EDGE,"E129.filletArc"),sQuery(id+"F1.wireOp",EDGE,"E130"),sQuery(id+"F1.wireOp",EDGE,"E131"),sQuery(id+"F1.wireOp",EDGE,"E132"),sQuery(id+"F1.wireOp",EDGE,"E133"),sQuery(id+"F1.wireOp",EDGE,"E134"),sQuery(id+"F1.wireOp",EDGE,"E135"),sQuery(id+"F1.wireOp",EDGE,"E136"),sQuery(id+"F1.wireOp",EDGE,"E137.filletArc"),sQuery(id+"F1.wireOp",EDGE,"E138.filletArc"),sQuery(id+"F1.wireOp",EDGE,"E139.filletArc"),sQuery(id+"F1.wireOp",EDGE,"E140.filletArc"),sQuery(id+"F1.wireOp",EDGE,"E141.bottom"),sQuery(id+"F1.wireOp",EDGE,"E141.top"),sQuery(id+"F1.wireOp",EDGE,"E141.left"),sQuery(id+"F1.wireOp",EDGE,"E141.right"),sQuery(id+"F1.wireOp",EDGE,"E142.filletArc"),sQuery(id+"F1.wireOp",EDGE,"E143.filletArc"),sQuery(id+"F1.wireOp",EDGE,"E144.filletArc"),sQuery(id+"F1.wireOp",EDGE,"E145.filletArc"),sQuery(id+"F1.wireOp",EDGE,"E146.bottom"),sQuery(id+"F1.wireOp",EDGE,"E146.top"),sQuery(id+"F1.wireOp",EDGE,"E146.left"),sQuery(id+"F1.wireOp",EDGE,"E146.right"),sQuery(id+"F1.wireOp",EDGE,"E147.filletArc"),sQuery(id+"F1.wireOp",EDGE,"E148.filletArc"),sQuery(id+"F1.wireOp",EDGE,"E149.filletArc"),sQuery(id+"F1.wireOp",EDGE,"E150.filletArc"),sQuery(id+"F1.wireOp",EDGE,"E151"),sQuery(id+"F1.wireOp",EDGE,"E152"),sQuery(id+"F1.wireOp",EDGE,"E153"),sQuery(id+"F1.wireOp",EDGE,"E154"),sQuery(id+"F1.wireOp",EDGE,"E155"),sQuery(id+"F1.wireOp",EDGE,"E156.filletArc"),sQuery(id+"F1.wireOp",EDGE,"E157.filletArc"),sQuery(id+"F1.wireOp",EDGE,"E158.filletArc"),sQuery(id+"F1.wireOp",EDGE,"E159.filletArc"),sQuery(id+"F1.wireOp",EDGE,"E160"),sQuery(id+"F1.wireOp",EDGE,"E161"),sQuery(id+"F1.wireOp",EDGE,"E162.bottom"),sQuery(id+"F1.wireOp",EDGE,"E162.top"),sQuery(id+"F1.wireOp",EDGE,"E162.left"),sQuery(id+"F1.wireOp",EDGE,"E162.right"),sQuery(id+"F1.wireOp",EDGE,"E163.filletArc"),sQuery(id+"F1.wireOp",EDGE,"E164.filletArc"),sQuery(id+"F1.wireOp",EDGE,"E165.filletArc"),sQuery(id+"F1.wireOp",EDGE,"E166.filletArc"),sQuery(id+"F1.wireOp",EDGE,"E167"),sQuery(id+"F1.wireOp",EDGE,"E168"),sQuery(id+"F1.wireOp",EDGE,"E169"),sQuery(id+"F1.wireOp",EDGE,"E170"),sQuery(id+"F1.wireOp",EDGE,"E171"),sQuery(id+"F1.wireOp",EDGE,"E172.filletArc"),sQuery(id+"F1.wireOp",EDGE,"E173.filletArc"),sQuery(id+"F1.wireOp",EDGE,"E174.filletArc"),sQuery(id+"F1.wireOp",EDGE,"E175.filletArc"),sQuery(id+"F1.wireOp",EDGE,"E176.filletArc"),sQuery(id+"F1.wireOp",EDGE,"E177"),sQuery(id+"F1.wireOp",EDGE,"E178"),sQuery(id+"F1.wireOp",EDGE,"E179"),sQuery(id+"F1.wireOp",EDGE,"E180.bottom"),sQuery(id+"F1.wireOp",EDGE,"E180.top"),sQuery(id+"F1.wireOp",EDGE,"E180.left"),sQuery(id+"F1.wireOp",EDGE,"E180.right"),sQuery(id+"F1.wireOp",EDGE,"E181"),sQuery(id+"F1.wireOp",EDGE,"E183.filletArc"),sQuery(id+"F1.wireOp",EDGE,"E184.filletArc"),sQuery(id+"F1.wireOp",EDGE,"E185"),sQuery(id+"F1.wireOp",EDGE,"E186"),sQuery(id+"F1.wireOp",EDGE,"E187.filletArc"),sQuery(id+"F1.wireOp",EDGE,"E188.filletArc"),sQuery(id+"F1.wireOp",EDGE,"E189.filletArc"),sQuery(id+"F1.wireOp",EDGE,"E190.filletArc"),sQuery(id+"F1.wireOp",EDGE,"E192"),sQuery(id+"F1.wireOp",EDGE,"E193"),sQuery(id+"F1.wireOp",EDGE,"E194"),sQuery(id+"F1.wireOp",EDGE,"E195")])]});
            var Q1;
            Q1=qCreatedBy(makeId("Front.planeOp"),FACE);
            mirror(context, id + "F3", {"entities" : qUnion([Q0]), "mirrorPlane" : qUnion([Q1])});
        }
        {
            var Q0;
            Q0=qCreatedBy(makeId("Top.planeOp"),FACE);
            var sketch = newSketch(context, id + "F4", { "sketchPlane" : qUnion([Q0])});
            skLineSegment(sketch, "E196.bottom", {"start": v(4155, 500) * mm, "end": v(11655, 500) * mm});
            skLineSegment(sketch, "E196.top", {"start": v(4155, -500) * mm, "end": v(11655, -500) * mm});
            skLineSegment(sketch, "E196.left", {"start": v(4155, 500) * mm, "end": v(4155, -500) * mm});
            skLineSegment(sketch, "E196.right", {"start": v(11655, 500) * mm, "end": v(11655, -500) * mm});
            skLineSegment(sketch, "E197", {"start": v(0, 0) * mm, "end": v(11655, 0) * mm, "construction": true});
            skLineSegment(sketch, "E198.bottom", {"start": v(4695, -350) * mm, "end": v(5435, -350) * mm});
            skLineSegment(sketch, "E198.top", {"start": v(4695, 350) * mm, "end": v(5435, 350) * mm});
            skLineSegment(sketch, "E198.left", {"start": v(4420, -75) * mm, "end": v(4420, 75) * mm});
            skLineSegment(sketch, "E198.right", {"start": v(5710, -75) * mm, "end": v(5710, 75) * mm});
            skLineSegment(sketch, "E199.bottom", {"start": v(6240, 300) * mm, "end": v(7490, 300) * mm});
            skLineSegment(sketch, "E199.top", {"start": v(6240, -300) * mm, "end": v(7490, -300) * mm});
            skLineSegment(sketch, "E199.left", {"start": v(5965, 25) * mm, "end": v(5965, -25) * mm});
            skLineSegment(sketch, "E199.right", {"start": v(7765, 25) * mm, "end": v(7765, -25) * mm});
            skLineSegment(sketch, "E200.bottom", {"start": v(8430, 300) * mm, "end": v(9500, 300) * mm});
            skLineSegment(sketch, "E200.top", {"start": v(8430, -300) * mm, "end": v(9500, -300) * mm});
            skLineSegment(sketch, "E200.left", {"start": v(8155, 25) * mm, "end": v(8155, -25) * mm});
            skLineSegment(sketch, "E200.right", {"start": v(9775, 25) * mm, "end": v(9775, -25) * mm});
            skLineSegment(sketch, "E201.bottom", {"start": v(10565, 300) * mm, "end": v(11075, 300) * mm});
            skLineSegment(sketch, "E201.top", {"start": v(10565, -300) * mm, "end": v(11075, -300) * mm});
            skLineSegment(sketch, "E201.left", {"start": v(10290, 25) * mm, "end": v(10290, -25) * mm});
            skLineSegment(sketch, "E201.right", {"start": v(11350, 25) * mm, "end": v(11350, -25) * mm});
            skPoint(sketch, "E202.visualSharp", {"position": v(4420, -350) * mm});
            skArc(sketch, "E202.filletArc", {"start": v(4420, -75) * mm, "mid": v(4500.55, -269.45) * mm, "end": v(4695, -350) * mm});
            skPoint(sketch, "E203.visualSharp", {"position": v(4420, 350) * mm});
            skArc(sketch, "E203.filletArc", {"start": v(4695, 350) * mm, "mid": v(4500.55, 269.45) * mm, "end": v(4420, 75) * mm});
            skPoint(sketch, "E204.visualSharp", {"position": v(5710, 350) * mm});
            skArc(sketch, "E204.filletArc", {"start": v(5710, 75) * mm, "mid": v(5629.45, 269.45) * mm, "end": v(5435, 350) * mm});
            skPoint(sketch, "E205.visualSharp", {"position": v(5710, -350) * mm});
            skArc(sketch, "E205.filletArc", {"start": v(5435, -350) * mm, "mid": v(5629.45, -269.45) * mm, "end": v(5710, -75) * mm});
            skPoint(sketch, "E206.visualSharp", {"position": v(5965, -300) * mm});
            skArc(sketch, "E206.filletArc", {"start": v(5965, -25) * mm, "mid": v(6045.55, -219.45) * mm, "end": v(6240, -300) * mm});
            skPoint(sketch, "E207.visualSharp", {"position": v(5965, 300) * mm});
            skArc(sketch, "E207.filletArc", {"start": v(6240, 300) * mm, "mid": v(6045.55, 219.45) * mm, "end": v(5965, 25) * mm});
            skPoint(sketch, "E208.visualSharp", {"position": v(7765, 300) * mm});
            skArc(sketch, "E208.filletArc", {"start": v(7765, 25) * mm, "mid": v(7684.45, 219.45) * mm, "end": v(7490, 300) * mm});
            skPoint(sketch, "E209.visualSharp", {"position": v(7765, -300) * mm});
            skArc(sketch, "E209.filletArc", {"start": v(7490, -300) * mm, "mid": v(7684.45, -219.45) * mm, "end": v(7765, -25) * mm});
            skPoint(sketch, "E210.visualSharp", {"position": v(8155, -300) * mm});
            skArc(sketch, "E210.filletArc", {"start": v(8155, -25) * mm, "mid": v(8235.55, -219.45) * mm, "end": v(8430, -300) * mm});
            skPoint(sketch, "E211.visualSharp", {"position": v(8155, 300) * mm});
            skArc(sketch, "E211.filletArc", {"start": v(8430, 300) * mm, "mid": v(8235.55, 219.45) * mm, "end": v(8155, 25) * mm});
            skPoint(sketch, "E212.visualSharp", {"position": v(9775, 300) * mm});
            skArc(sketch, "E212.filletArc", {"start": v(9775, 25) * mm, "mid": v(9694.45, 219.45) * mm, "end": v(9500, 300) * mm});
            skPoint(sketch, "E213.visualSharp", {"position": v(9775, -300) * mm});
            skArc(sketch, "E213.filletArc", {"start": v(9500, -300) * mm, "mid": v(9694.45, -219.45) * mm, "end": v(9775, -25) * mm});
            skPoint(sketch, "E214.visualSharp", {"position": v(10290, -300) * mm});
            skArc(sketch, "E214.filletArc", {"start": v(10290, -25) * mm, "mid": v(10370.55, -219.45) * mm, "end": v(10565, -300) * mm});
            skPoint(sketch, "E215.visualSharp", {"position": v(10290, 300) * mm});
            skArc(sketch, "E215.filletArc", {"start": v(10565, 300) * mm, "mid": v(10370.55, 219.45) * mm, "end": v(10290, 25) * mm});
            skPoint(sketch, "E216.visualSharp", {"position": v(11350, 300) * mm});
            skArc(sketch, "E216.filletArc", {"start": v(11350, 25) * mm, "mid": v(11269.45, 219.45) * mm, "end": v(11075, 300) * mm});
            skPoint(sketch, "E217.visualSharp", {"position": v(11350, -300) * mm});
            skArc(sketch, "E217.filletArc", {"start": v(11075, -300) * mm, "mid": v(11269.45, -219.45) * mm, "end": v(11350, -25) * mm});
            skSolve(sketch);
        }
        {
            var Q0;
            Q0=makeQuery(id+"F4.imprint","IMPRINT",FACE,{"disambiguationData":[TD([[makeQuery(id+"F4.imprint","IMPRINT",EDGE,{"derivedFrom":sQuery(id+"F4.wireOp",EDGE,"E196.bottom")}),-1.0]])]});
            extrude(context, id + "F5", {"entities" : qUnion([Q0]), "depth" : 1450 * mm, "offsetDistance" : 25 * mm, "hasSecondDirection" : true, "secondDirectionOppositeDirection" : false, "secondDirectionDepth" : 1360 * mm});
        }
    });
